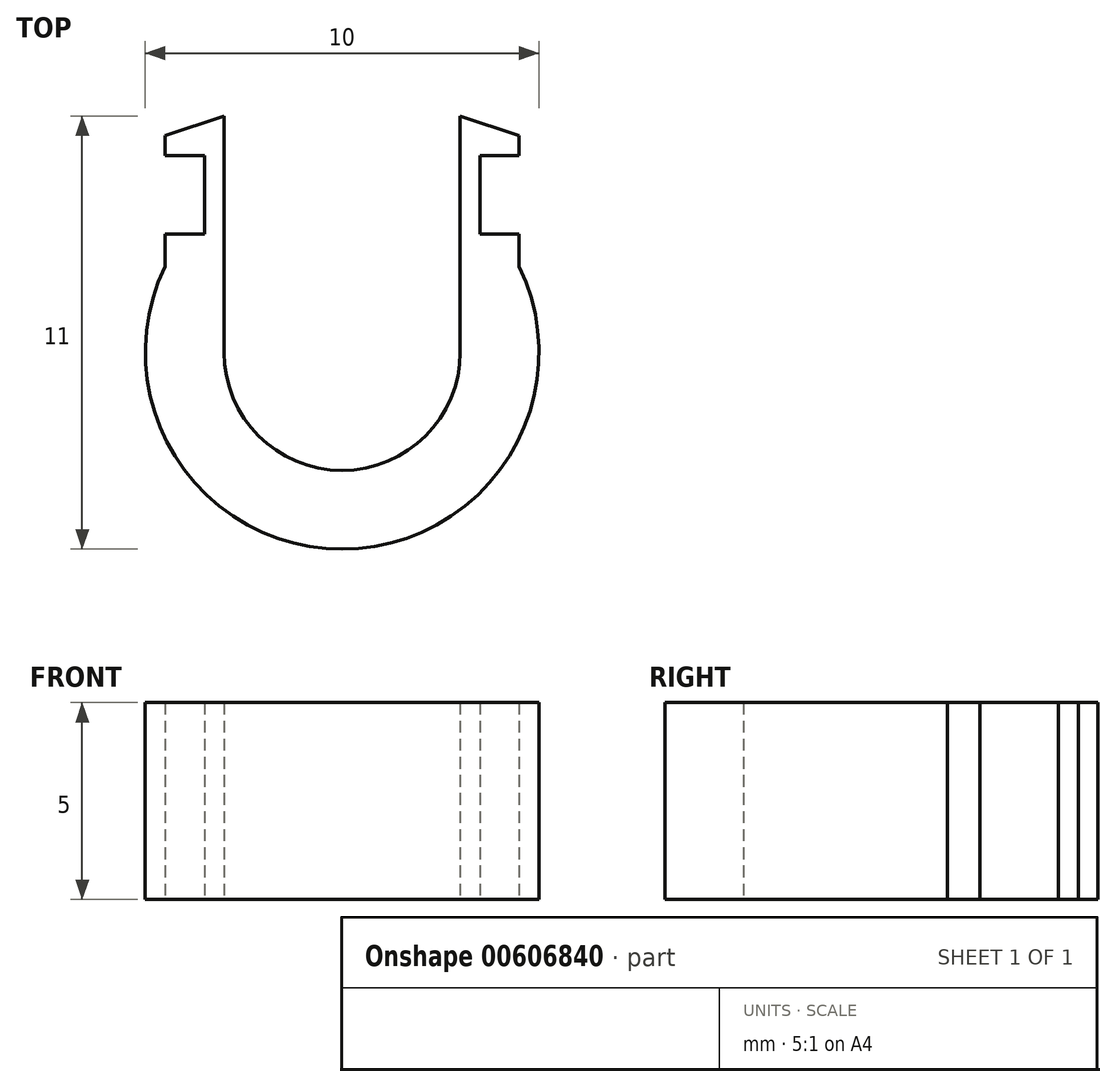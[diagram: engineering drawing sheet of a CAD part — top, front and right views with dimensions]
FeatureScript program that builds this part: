
annotation { "Feature Type Name" : "Feature", "Feature Type Description" : "" }
export const myFeature = defineFeature(function(context is Context, id is Id, definition is map)
    precondition{}
    {
        {
            var Q0;
            Q0=qCreatedBy(makeId("Top.planeOp"),FACE);
            var sketch = newSketch(context, id + "F0", { "sketchPlane" : qUnion([Q0])});
            skArc(sketch, "E0", {"start": v(-4.5, 2.18) * mm, "mid": v(0, -5) * mm, "end": v(4.5, 2.18) * mm});
            skArc(sketch, "E1", {"start": v(-3, 0) * mm, "mid": v(0, -3) * mm, "end": v(3, 0) * mm});
            skLineSegment(sketch, "E2", {"start": v(-3, 0) * mm, "end": v(-3, 6) * mm});
            skLineSegment(sketch, "E3", {"start": v(-3, 6) * mm, "end": v(-4.5, 5.5) * mm});
            skLineSegment(sketch, "E4", {"start": v(-4.5, 5.5) * mm, "end": v(-4.5, 5) * mm});
            skLineSegment(sketch, "E5", {"start": v(-4.5, 5) * mm, "end": v(-3.5, 5) * mm});
            skLineSegment(sketch, "E6", {"start": v(-3.5, 5) * mm, "end": v(-3.5, 3) * mm});
            skLineSegment(sketch, "E7", {"start": v(-3.5, 3) * mm, "end": v(-4.5, 3) * mm});
            skLineSegment(sketch, "E8", {"start": v(-4.5, 3) * mm, "end": v(-4.5, 2.18) * mm});
            skLineSegment(sketch, "E9.MirrorCS", {"start": v(3, 0) * mm, "end": v(3, 6) * mm});
            skLineSegment(sketch, "E10.MirrorCS", {"start": v(3, 6) * mm, "end": v(4.5, 5.5) * mm});
            skLineSegment(sketch, "E11.MirrorCS", {"start": v(4.5, 5.5) * mm, "end": v(4.5, 5) * mm});
            skLineSegment(sketch, "E12.MirrorCS", {"start": v(4.5, 5) * mm, "end": v(3.5, 5) * mm});
            skLineSegment(sketch, "E13.MirrorCS", {"start": v(3.5, 5) * mm, "end": v(3.5, 3) * mm});
            skLineSegment(sketch, "E14.MirrorCS", {"start": v(3.5, 3) * mm, "end": v(4.5, 3) * mm});
            skLineSegment(sketch, "E15.MirrorCS", {"start": v(4.5, 3) * mm, "end": v(4.5, 2.18) * mm});
            skSolve(sketch);
        }
        {
            var Q0;
            Q0 = qSketchRegion(id + "F0", true);
            extrude(context, id + "F1", {"entities" : qUnion([Q0]), "depth" : 5 * mm, "offsetDistance" : 25 * mm});
        }
    });
